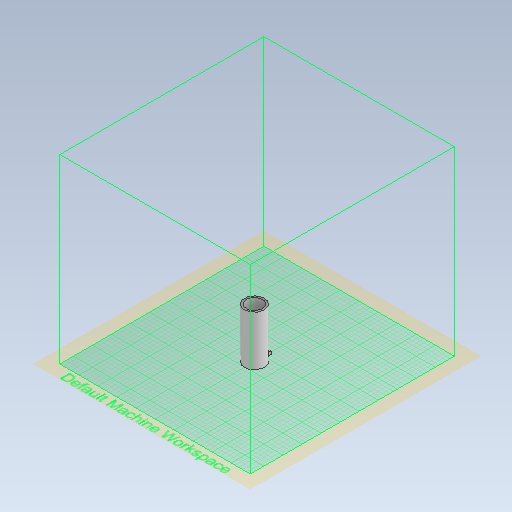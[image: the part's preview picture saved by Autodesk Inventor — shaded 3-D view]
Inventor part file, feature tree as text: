
AUTODESK INVENTOR PART (.ipt)
format: ipt  version: 2021 (Build 250183000, 183)  size: 576,512 bytes
history: native  units: in
note: dims shown in document units (in); Inventor stores cm internally (conversion verified against a paired STEP export)
features: projected_geometry x11, extrude x9, sketch x5, chamfer x3, fillet x2, plane x1, pattern_linear x1
ambient origin geometry x8: Origin, YZ Plane, XZ Plane, XY Plane, X Axis, Y Axis, Z Axis, Center Point
bodies: Solid1 (feature_tree)
feature tree (32):
  extrude  "Extrusion1"  Depth=3.2677in TaperAngle=0.0deg
  plane  "Work Plane1"
  extrude  "Extrusion7"  Depth=3.189in TaperAngle=0.0deg
  extrude  "Extrusion8"  Depth=0.3937in
  extrude  "Extrusion9"  Depth=0.3937in
  extrude  "Extrusion10"  Depth=0.3937in TaperAngle=0.0deg
  extrude  "Extrusion11"  Depth=0.3937in
  extrude  "Extrusion12"  Depth=0.3937in
  pattern_linear  "Rectangular Pattern3"  Spacing1=0.1969in  [1 undecoded]
  extrude  "Extrusion13"  Depth=0.3937in TaperAngle=0.0deg
  chamfer  "Chamfer2"  Distance=1.811in
  chamfer  "Chamfer4"  Distance=0.0394in
  chamfer  "Chamfer5"  Distance=0.0098in
  extrude  "Extrusion14"  Depth=0.0787in
  fillet  "Fillet11"  Radius=0.1181in
  fillet  "Fillet12"  Radius=0.3937in
  sketch  "Sketch2"  dims[d2=1.752in d3=3.2677in d4=0.0in]
  sketch  "Sketch9"  dims[d54=1.4173in d55=3.189in d56=0.0in]
  projected_geometry  "Projected Loop7"
  sketch  "Sketch10"  dims[d57=0.3937in d58=0.2756in]
  projected_geometry  "Projected Loop8"
  projected_geometry  "Projected Loop9"
  projected_geometry  "Projected Loop10"
  projected_geometry  "Projected Loop11"
  projected_geometry  "Projected Loop12"
  projected_geometry  "Projected Loop14"
  projected_geometry  "Projected Loop15"
  sketch  "Sketch16"  dims[d59=0.3937in d60=0.0236in d61=0.0in d62=0.0in d63=0.2047in]
  projected_geometry  "Projected Loop16"
  sketch  "Sketch17"  dims[d64=0.126in d66=0.0295in d67=0.0in d68=0.0591in d69=0.0591in d71=0.1969in d72=0.0in d76=1.1811in d77=0.0in d84=1.811in d85=0.0394in d86=0.0098in d87=0.0in d88=8.2677in d90=0.0787in d92=0.1181in d93=0.3937in d94=0.0in d96=0.0059in d97=0.0185in d98=0.0787in d99=45.0deg d103=0.1575in d104=0.0787in d105=45.0deg d106=0.0098in d107=0.0787in d108=45.0deg d109=0.2756in d110=0.0315in d111=0.0in d116=0.4724in d117=0.3937in d19=0.0197in d20=0.0344in d21=0.0197in d22=0.0344in]
  projected_geometry  "Projected Loop17"
  projected_geometry  "Projected Loop18"
note: 1 required parameter value undecoded (feature->parameter linkage not recoverable at this tier; creation-order binding heuristic only, values carry confidence <= 0.55)
